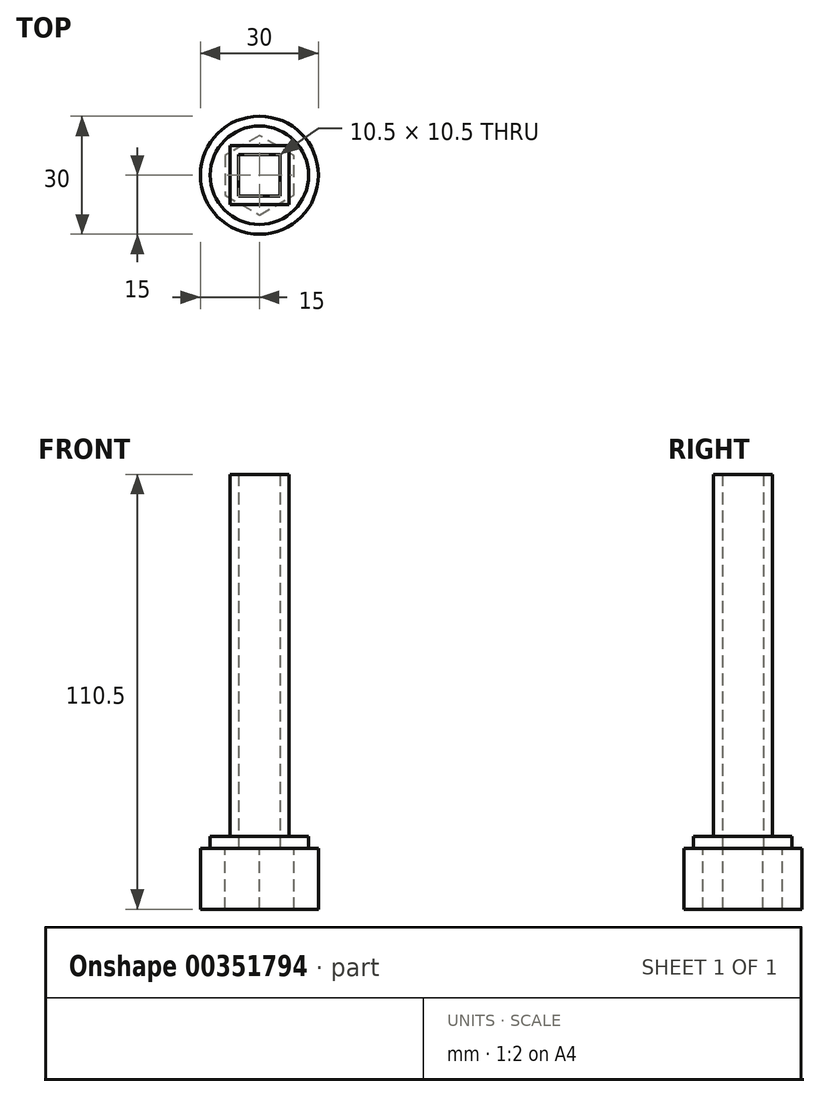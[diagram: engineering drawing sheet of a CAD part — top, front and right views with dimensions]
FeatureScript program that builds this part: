
annotation { "Feature Type Name" : "Feature", "Feature Type Description" : "" }
export const myFeature = defineFeature(function(context is Context, id is Id, definition is map)
    precondition{}
    {
        {
            var Q0;
            Q0=qCreatedBy(makeId("Top.planeOp"),FACE);
            var sketch = newSketch(context, id + "F0", { "sketchPlane" : qUnion([Q0])});
            skLineSegment(sketch, "E0.bottom", {"start": v(5.25, 5.25) * mm, "end": v(-5.25, 5.25) * mm});
            skLineSegment(sketch, "E0.top", {"start": v(5.25, -5.25) * mm, "end": v(-5.25, -5.25) * mm});
            skLineSegment(sketch, "E0.left", {"start": v(5.25, 5.25) * mm, "end": v(5.25, -5.25) * mm});
            skLineSegment(sketch, "E0.right", {"start": v(-5.25, 5.25) * mm, "end": v(-5.25, -5.25) * mm});
            skPoint(sketch, "E0.middle", {"position": v(0, 0) * mm});
            skLineSegment(sketch, "E1.bottom", {"start": v(7.5, 7.5) * mm, "end": v(-7.5, 7.5) * mm});
            skLineSegment(sketch, "E1.top", {"start": v(7.5, -7.5) * mm, "end": v(-7.5, -7.5) * mm});
            skLineSegment(sketch, "E1.left", {"start": v(7.5, 7.5) * mm, "end": v(7.5, -7.5) * mm});
            skLineSegment(sketch, "E1.right", {"start": v(-7.5, 7.5) * mm, "end": v(-7.5, -7.5) * mm});
            skSolve(sketch);
        }
        {
            var Q0;
            Q0 = qSketchRegion(id + "F0", true);
            extrude(context, id + "F1", {"entities" : qUnion([Q0]), "depth" : 95 * mm});
        }
        {
            var Q0;
            Q0=makeQuery(id+"F1.opExtrude","CAP_FACE",FACE,{"disambiguationData":[OSD([sQuery(id+"F0.wireOp",EDGE,"E0.bottom"),sQuery(id+"F0.wireOp",EDGE,"E0.top"),sQuery(id+"F0.wireOp",EDGE,"E0.left"),sQuery(id+"F0.wireOp",EDGE,"E0.right"),sQuery(id+"F0.wireOp",EDGE,"E1.bottom"),sQuery(id+"F0.wireOp",EDGE,"E1.top"),sQuery(id+"F0.wireOp",EDGE,"E1.left"),sQuery(id+"F0.wireOp",EDGE,"E1.right")])],"isStart":true});
            var sketch = newSketch(context, id + "F2", { "sketchPlane" : qUnion([Q0])});
            skCircle(sketch, "E2", {"center": v(0, 0) * mm, "radius": 15 * mm});
            skCircle(sketch, "E3.cCircle", {"center": v(0, 0) * mm, "radius": 8.75 * mm, "construction": true});
            skPoint(sketch, "E3.cCircle.perimeterSnap0", {"position": v(-7.5, 0) * mm});
            skLineSegment(sketch, "E3.0", {"start": v(-8.75, -5.05) * mm, "end": v(-8.75, 5.05) * mm});
            skLineSegment(sketch, "E3.1", {"start": v(-8.75, 5.05) * mm, "end": v(0, 10.1) * mm});
            skLineSegment(sketch, "E3.2", {"start": v(0, 10.1) * mm, "end": v(8.75, 5.05) * mm});
            skLineSegment(sketch, "E3.3", {"start": v(8.75, 5.05) * mm, "end": v(8.75, -5.05) * mm});
            skLineSegment(sketch, "E3.4", {"start": v(8.75, -5.05) * mm, "end": v(0, -10.1) * mm});
            skLineSegment(sketch, "E3.5", {"start": v(0, -10.1) * mm, "end": v(-8.75, -5.05) * mm});
            skPoint(sketch, "E3.0.midPoint", {"position": v(-8.75, 0) * mm});
            skPoint(sketch, "E3.0.midPoint.positionSnap0", {"position": v(-7.5, 0) * mm});
            skSolve(sketch);
        }
        {
            var Q0;
            Q0 = qSketchRegion(id + "F2", true);
            extrude(context, id + "F3", {"entities" : qUnion([Q0]), "operationType" : NewBodyOperationType.ADD, "depth" : 15.5 * mm});
        }
        {
            var Q0;
            Q0=makeQuery(id+"F3.opExtrude","CAP_FACE",FACE,{"disambiguationData":[OSD([sQuery(id+"F2.wireOp",EDGE,"E2"),sQuery(id+"F2.wireOp",EDGE,"E3.0"),sQuery(id+"F2.wireOp",EDGE,"E3.1"),sQuery(id+"F2.wireOp",EDGE,"E3.2"),sQuery(id+"F2.wireOp",EDGE,"E3.3"),sQuery(id+"F2.wireOp",EDGE,"E3.4"),sQuery(id+"F2.wireOp",EDGE,"E3.5")])],"isStart":true});
            var sketch = newSketch(context, id + "F4", { "sketchPlane" : qUnion([Q0])});
            skCircle(sketch, "E4", {"center": v(0, 0) * mm, "radius": 12.5 * mm});
            skLineSegment(sketch, "E5.bottom", {"start": v(-7.5, -7.5) * mm, "end": v(7.5, -7.5) * mm});
            skLineSegment(sketch, "E5.top", {"start": v(-7.5, 7.5) * mm, "end": v(7.5, 7.5) * mm});
            skLineSegment(sketch, "E5.left", {"start": v(-7.5, -7.5) * mm, "end": v(-7.5, 7.5) * mm});
            skLineSegment(sketch, "E5.right", {"start": v(7.5, -7.5) * mm, "end": v(7.5, 7.5) * mm});
            skSolve(sketch);
        }
        {
            var Q0;
            Q0 = qSketchRegion(id + "F4", true);
            extrude(context, id + "F5", {"entities" : qUnion([Q0]), "operationType" : NewBodyOperationType.ADD, "depth" : 3 * mm});
        }
    });
